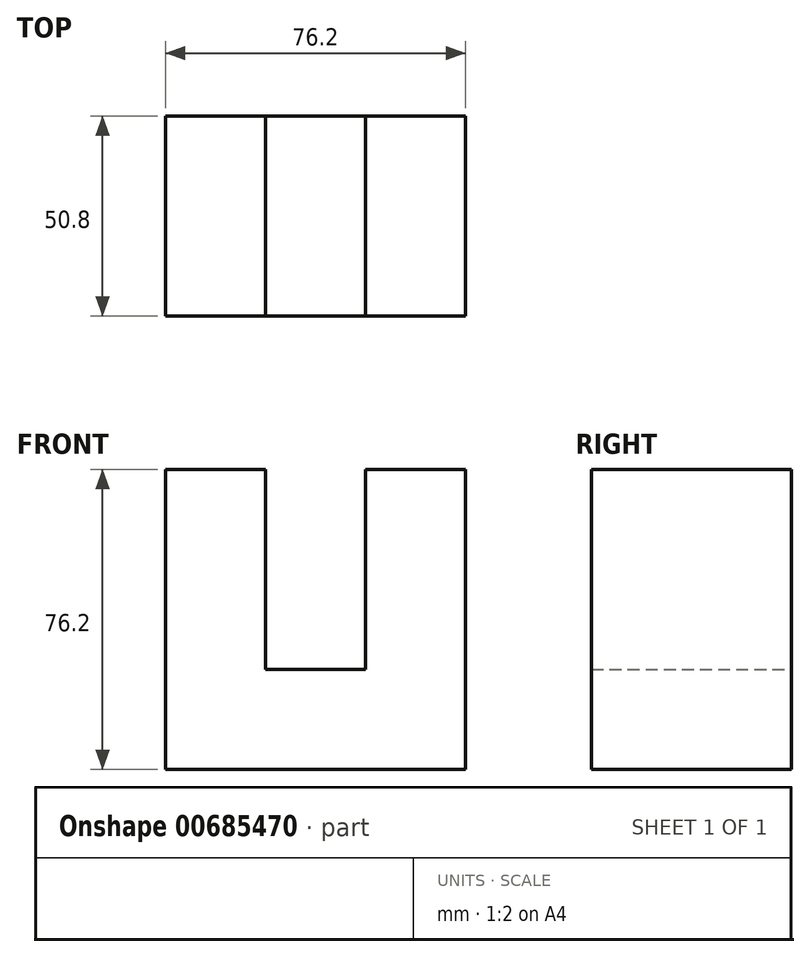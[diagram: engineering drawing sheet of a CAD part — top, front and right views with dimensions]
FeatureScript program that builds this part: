
annotation { "Feature Type Name" : "Feature", "Feature Type Description" : "" }
export const myFeature = defineFeature(function(context is Context, id is Id, definition is map)
    precondition{}
    {
        {
            var Q0;
            Q0=qCreatedBy(makeId("Front.planeOp"),FACE);
            var sketch = newSketch(context, id + "F0", { "sketchPlane" : qUnion([Q0])});
            skLineSegment(sketch, "E0", {"start": v(-50.8, 35.62) * mm, "end": v(-50.8, -40.58) * mm});
            skLineSegment(sketch, "E1", {"start": v(-50.8, -40.58) * mm, "end": v(25.4, -40.58) * mm});
            skLineSegment(sketch, "E2", {"start": v(25.4, -40.58) * mm, "end": v(25.4, 35.62) * mm});
            skLineSegment(sketch, "E3", {"start": v(25.4, 35.62) * mm, "end": v(0, 35.62) * mm});
            skLineSegment(sketch, "E4", {"start": v(0, 35.62) * mm, "end": v(0, -15.18) * mm});
            skLineSegment(sketch, "E5", {"start": v(0, -15.18) * mm, "end": v(-25.4, -15.18) * mm});
            skLineSegment(sketch, "E6", {"start": v(-25.4, -15.18) * mm, "end": v(-25.4, 35.62) * mm});
            skLineSegment(sketch, "E7", {"start": v(-25.4, 35.62) * mm, "end": v(-50.8, 35.62) * mm});
            skSolve(sketch);
        }
        {
            var Q0;
            Q0=makeQuery(id+"F0.imprint","IMPRINT",FACE,{"disambiguationData":[TD([[makeQuery(id+"F0.imprint","IMPRINT",EDGE,{"derivedFrom":sQuery(id+"F0.wireOp",EDGE,"E0")}),1.0]])]});
            extrude(context, id + "F1", {"entities" : qUnion([Q0]), "depth" : 50.8 * mm, "offsetDistance" : 25.4 * mm});
        }
    });
